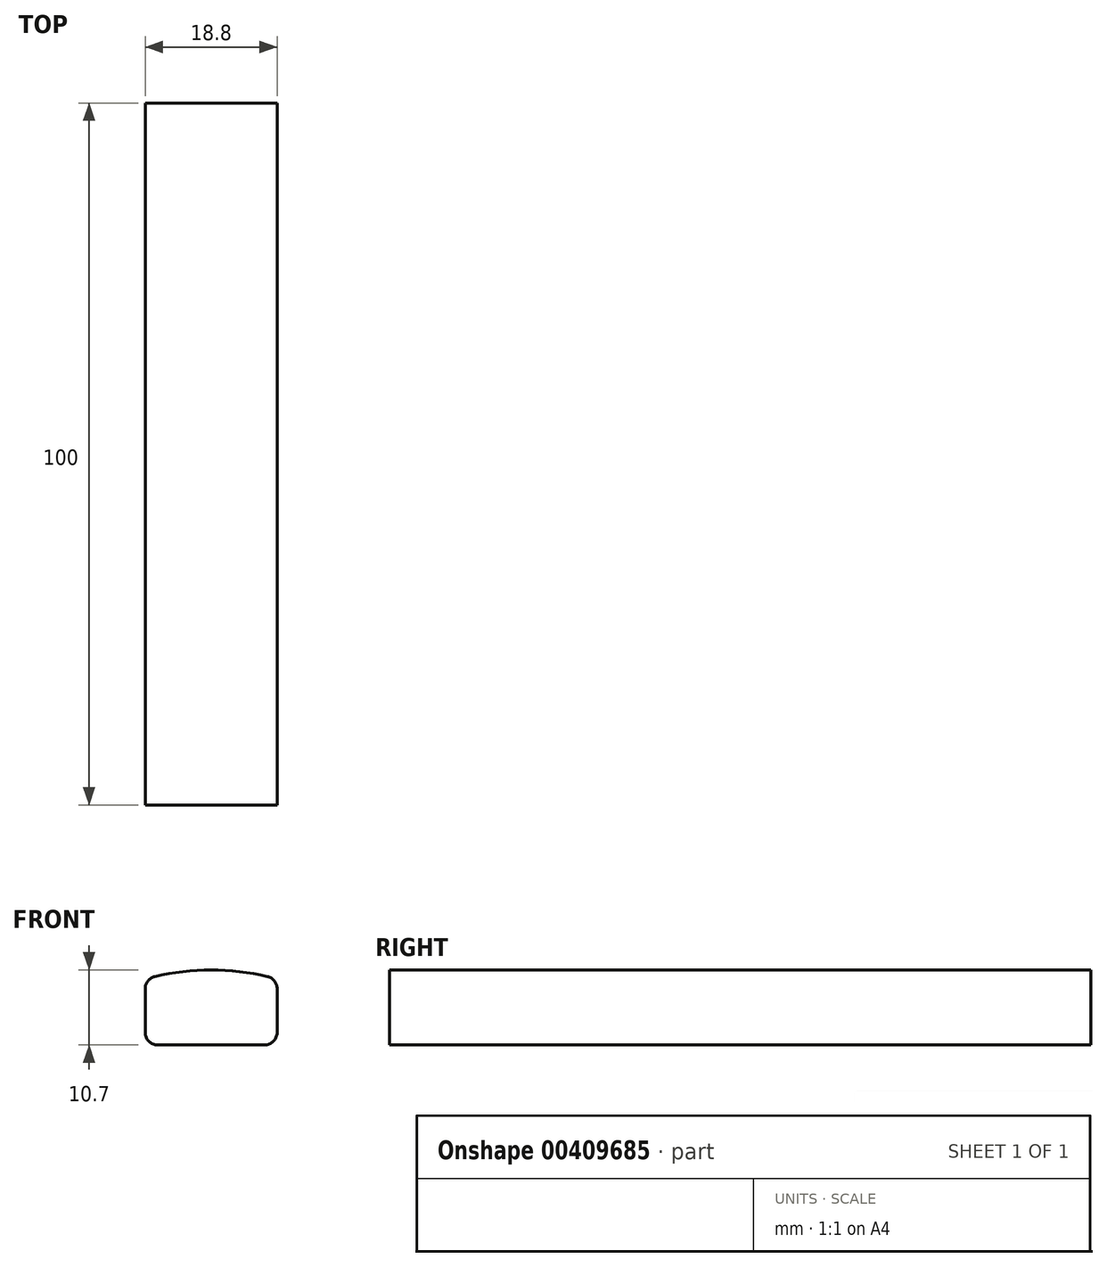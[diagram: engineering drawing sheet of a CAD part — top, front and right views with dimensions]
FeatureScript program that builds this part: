
annotation { "Feature Type Name" : "Feature", "Feature Type Description" : "" }
export const myFeature = defineFeature(function(context is Context, id is Id, definition is map)
    precondition{}
    {
        {
            var Q0;
            Q0=qCreatedBy(makeId("Front.planeOp"),FACE);
            var sketch = newSketch(context, id + "F0", { "sketchPlane" : qUnion([Q0])});
            skLineSegment(sketch, "E0.top", {"start": v(-7.6, -4.7) * mm, "end": v(7.6, -4.7) * mm});
            skLineSegment(sketch, "E0.left", {"start": v(-9.4, 3.3) * mm, "end": v(-9.4, -2.9) * mm});
            skLineSegment(sketch, "E0.right", {"start": v(9.4, 3.3) * mm, "end": v(9.4, -2.9) * mm});
            skPoint(sketch, "E0.middle", {"position": v(0, 0) * mm});
            skArc(sketch, "E1", {"start": v(-8.02, 5.06) * mm, "mid": v(0, 6) * mm, "end": v(8.02, 5.06) * mm});
            skPoint(sketch, "E2", {"position": v(0, 6) * mm});
            skPoint(sketch, "E3", {"position": v(0, -4.7) * mm});
            skPoint(sketch, "E4.visualSharp", {"position": v(-9.4, 4.7) * mm});
            skArc(sketch, "E4.filletArc", {"start": v(-8.02, 5.06) * mm, "mid": v(-9.01, 4.42) * mm, "end": v(-9.4, 3.3) * mm});
            skPoint(sketch, "E5.visualSharp", {"position": v(9.4, 4.7) * mm});
            skArc(sketch, "E5.filletArc", {"start": v(9.4, 3.3) * mm, "mid": v(9.01, 4.42) * mm, "end": v(8.02, 5.06) * mm});
            skPoint(sketch, "E6.visualSharp", {"position": v(-9.4, -4.7) * mm});
            skArc(sketch, "E6.filletArc", {"start": v(-9.4, -2.9) * mm, "mid": v(-8.87, -4.17) * mm, "end": v(-7.6, -4.7) * mm});
            skPoint(sketch, "E7.visualSharp", {"position": v(9.4, -4.7) * mm});
            skArc(sketch, "E7.filletArc", {"start": v(7.6, -4.7) * mm, "mid": v(8.87, -4.17) * mm, "end": v(9.4, -2.9) * mm});
            skSolve(sketch);
        }
        {
            var Q0;
            Q0 = qSketchRegion(id + "F0", true);
            extrude(context, id + "F1", {"entities" : qUnion([Q0]), "depth" : 100 * mm});
        }
    });
